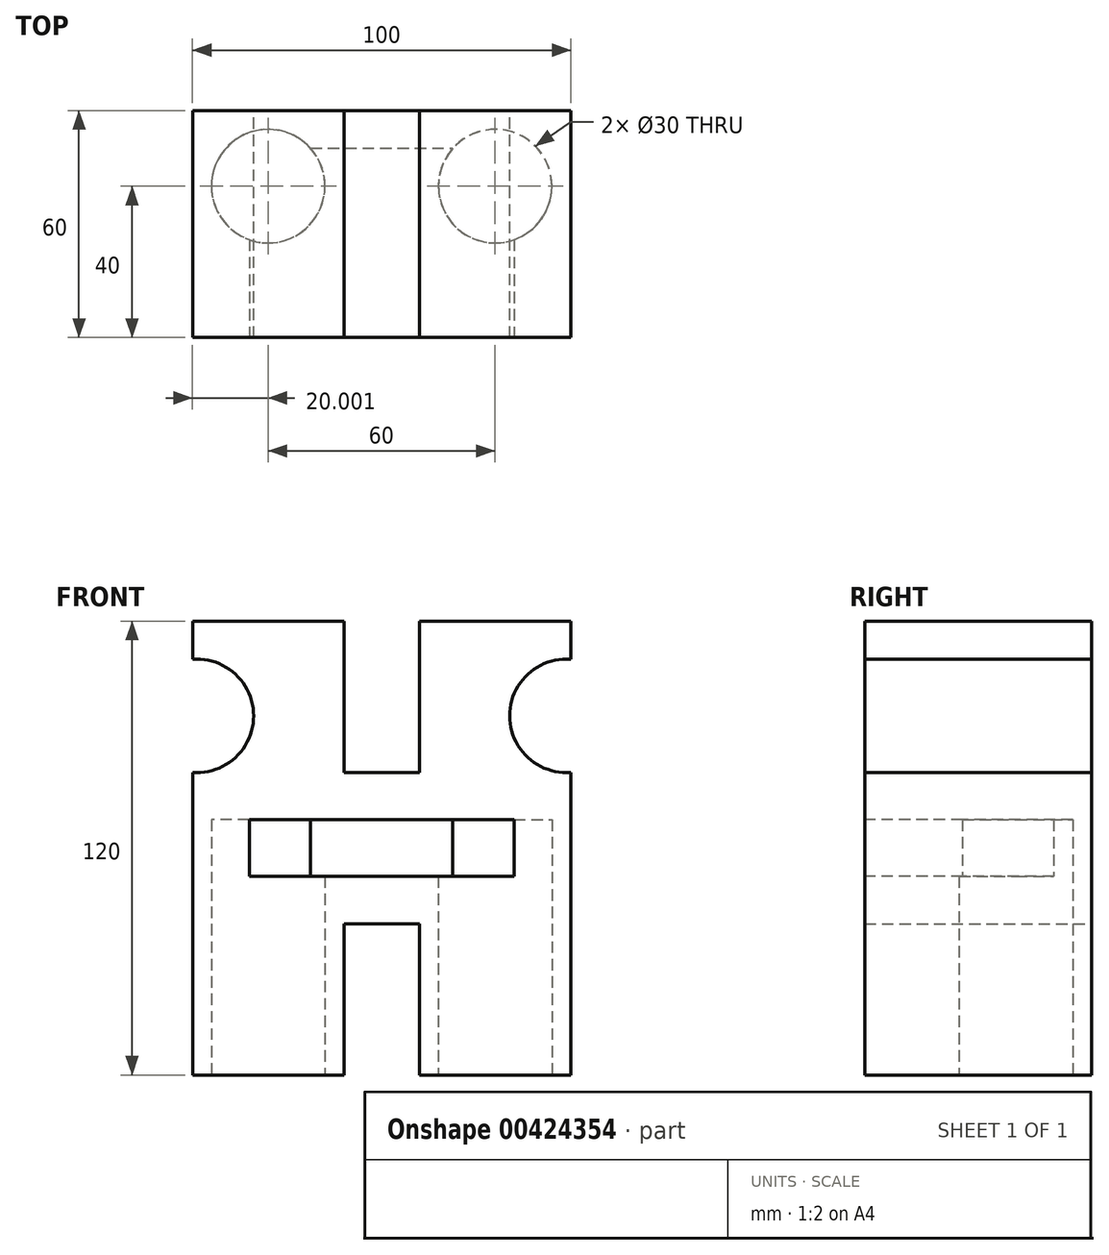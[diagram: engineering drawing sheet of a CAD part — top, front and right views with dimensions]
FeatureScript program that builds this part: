
annotation { "Feature Type Name" : "Feature", "Feature Type Description" : "" }
export const myFeature = defineFeature(function(context is Context, id is Id, definition is map)
    precondition{}
    {
        {
            var Q0;
            Q0=qCreatedBy(makeId("Front.planeOp"),FACE);
            var sketch = newSketch(context, id + "F0", { "sketchPlane" : qUnion([Q0])});
            skLineSegment(sketch, "E0.bottom", {"start": v(-48.04, 59.25) * mm, "end": v(-8.04, 59.25) * mm});
            skLineSegment(sketch, "E0.top", {"start": v(-48.04, -60.75) * mm, "end": v(-8.04, -60.75) * mm});
            skLineSegment(sketch, "E0.left", {"start": v(-48.04, 19.25) * mm, "end": v(-48.04, -60.75) * mm});
            skLineSegment(sketch, "E0.right", {"start": v(51.96, 19.25) * mm, "end": v(51.96, -60.75) * mm});
            skLineSegment(sketch, "E1", {"start": v(-8.04, 59.25) * mm, "end": v(-8.04, 19.25) * mm});
            skLineSegment(sketch, "E2", {"start": v(-8.04, 19.25) * mm, "end": v(11.96, 19.25) * mm});
            skLineSegment(sketch, "E3", {"start": v(11.96, 19.25) * mm, "end": v(11.96, 59.25) * mm});
            skLineSegment(sketch, "E4", {"start": v(11.96, -60.75) * mm, "end": v(11.96, -20.75) * mm});
            skLineSegment(sketch, "E5", {"start": v(11.96, -20.75) * mm, "end": v(-8.04, -20.75) * mm});
            skLineSegment(sketch, "E6", {"start": v(-8.04, -20.75) * mm, "end": v(-8.04, -60.75) * mm});
            skLineSegment(sketch, "E7.trimOffspring", {"start": v(11.96, -60.75) * mm, "end": v(51.96, -60.75) * mm});
            skLineSegment(sketch, "E8.trimOffspring", {"start": v(11.96, 59.25) * mm, "end": v(51.96, 59.25) * mm});
            skLineSegment(sketch, "E9", {"start": v(11.96, 19.25) * mm, "end": v(-8.04, 19.25) * mm});
            skLineSegment(sketch, "E10", {"start": v(-48.04, 59.25) * mm, "end": v(-48.04, 49.16) * mm});
            skLineSegment(sketch, "E11", {"start": v(51.96, 59.25) * mm, "end": v(51.96, 49.16) * mm});
            skArc(sketch, "E12", {"start": v(-48.04, 19.25) * mm, "mid": v(-31.88, 34.2) * mm, "end": v(-48.04, 49.16) * mm});
            skArc(sketch, "E13", {"start": v(51.96, 49.16) * mm, "mid": v(35.8, 34.2) * mm, "end": v(51.96, 19.25) * mm});
            skSolve(sketch);
        }
        {
            var Q0;
            Q0=makeQuery(id+"F0.imprint","IMPRINT",FACE,{"disambiguationData":[TD([[makeQuery(id+"F0.imprint","IMPRINT",EDGE,{"derivedFrom":sQuery(id+"F0.wireOp",EDGE,"E0.bottom")}),-1.0]])]});
            extrude(context, id + "F1", {"entities" : qUnion([Q0]), "depth" : 60 * mm});
        }
        {
            var Q0;
            Q0=makeQuery(id+"F1.opExtrude","CAP_FACE",FACE,{"disambiguationData":[OSD([sQuery(id+"F0.wireOp",EDGE,"E0.bottom"),sQuery(id+"F0.wireOp",EDGE,"E0.top"),sQuery(id+"F0.wireOp",EDGE,"E0.left"),sQuery(id+"F0.wireOp",EDGE,"E0.right"),sQuery(id+"F0.wireOp",EDGE,"E1"),sQuery(id+"F0.wireOp",EDGE,"E2"),sQuery(id+"F0.wireOp",EDGE,"E3"),sQuery(id+"F0.wireOp",EDGE,"E4"),sQuery(id+"F0.wireOp",EDGE,"E5"),sQuery(id+"F0.wireOp",EDGE,"E6"),sQuery(id+"F0.wireOp",EDGE,"E7.trimOffspring"),sQuery(id+"F0.wireOp",EDGE,"E8.trimOffspring")])],"isStart":false});
            var sketch = newSketch(context, id + "F2", { "sketchPlane" : qUnion([Q0])});
            skLineSegment(sketch, "E14.bottom", {"start": v(-33.04, 6.75) * mm, "end": v(36.96, 6.75) * mm});
            skLineSegment(sketch, "E14.top", {"start": v(-33.04, -8.25) * mm, "end": v(36.96, -8.25) * mm});
            skLineSegment(sketch, "E14.left", {"start": v(-33.04, 6.75) * mm, "end": v(-33.04, -8.25) * mm});
            skLineSegment(sketch, "E14.right", {"start": v(36.96, 6.75) * mm, "end": v(36.96, -8.25) * mm});
            skSolve(sketch);
        }
        {
            var Q0;
            Q0=makeQuery(id+"F2.imprint","IMPRINT",FACE,{"disambiguationData":[TD([[makeQuery(id+"F2.imprint","IMPRINT",EDGE,{"derivedFrom":sQuery(id+"F2.wireOp",EDGE,"E14.bottom")}),-1.0]])]});
            extrude(context, id + "F3", {"entities" : qUnion([Q0]), "operationType" : NewBodyOperationType.REMOVE, "oppositeDirection" : true, "depth" : 50 * mm});
        }
        {
            var Q0;
            Q0=makeQuery(id+"F1.opExtrude","SWEPT_FACE",FACE,{"disambiguationData":[OSD([sQuery(id+"F0.wireOp",EDGE,"E0.top")])]});
            var sketch = newSketch(context, id + "F4", { "sketchPlane" : qUnion([Q0])});
            skCircle(sketch, "E15", {"center": v(-28.04, 20) * mm, "radius": 15 * mm});
            skSolve(sketch);
        }
        {
            var Q0;
            Q0=makeQuery(id+"F1.opExtrude","SWEPT_FACE",FACE,{"disambiguationData":[OSD([sQuery(id+"F0.wireOp",EDGE,"E7.trimOffspring")])]});
            var sketch = newSketch(context, id + "F5", { "sketchPlane" : qUnion([Q0])});
            skCircle(sketch, "E16", {"center": v(31.96, 20) * mm, "radius": 15 * mm});
            skSolve(sketch);
        }
        {
            var Q0;
            Q0=makeQuery(id+"F4.imprint","IMPRINT",FACE,{"disambiguationData":[TD([[makeQuery(id+"F4.imprint","IMPRINT",EDGE,{"derivedFrom":sQuery(id+"F4.wireOp",EDGE,"E15")}),1.0]])]});
            var Q1;
            Q1=makeQuery(id+"F5.imprint","IMPRINT",FACE,{"disambiguationData":[TD([[makeQuery(id+"F5.imprint","IMPRINT",EDGE,{"derivedFrom":sQuery(id+"F5.wireOp",EDGE,"E16")}),1.0]])]});
            var Q2;
            Q2=sQuery(id+"F4.wireOp",EDGE,"E15");
            extrude(context, id + "F6", {"entities" : qUnion([Q0, Q1]), "operationType" : NewBodyOperationType.REMOVE, "surfaceEntities" : qUnion([Q2]), "oppositeDirection" : true, "depth" : 67.5 * mm});
        }
    });
